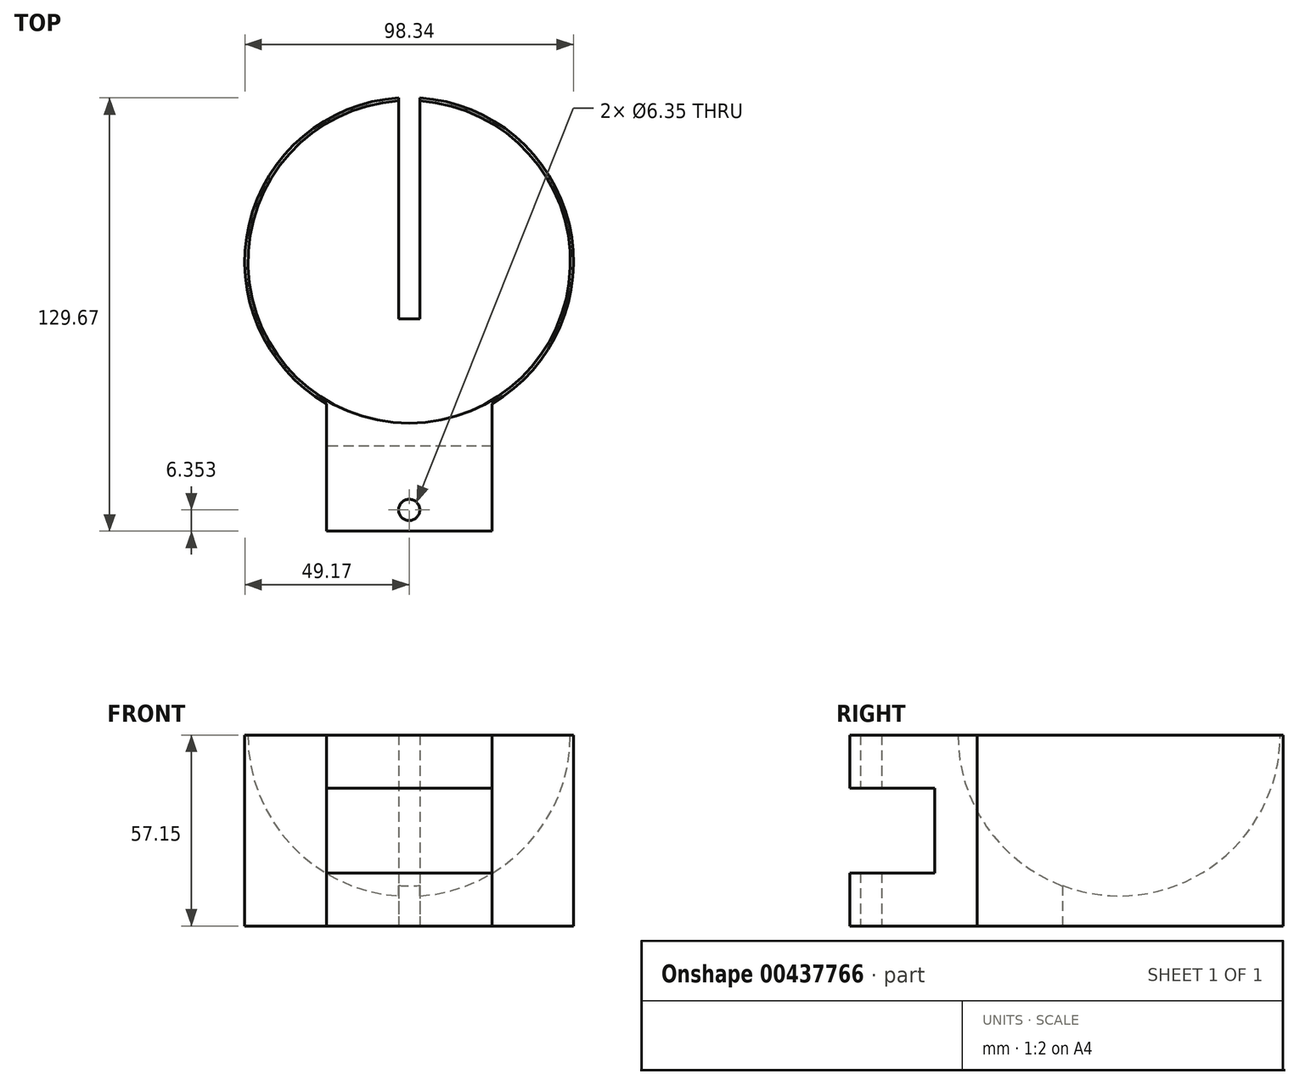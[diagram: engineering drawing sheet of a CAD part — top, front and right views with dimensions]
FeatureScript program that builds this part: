
annotation { "Feature Type Name" : "Feature", "Feature Type Description" : "" }
export const myFeature = defineFeature(function(context is Context, id is Id, definition is map)
    precondition{}
    {
        {
            var Q0;
            Q0=qCreatedBy(makeId("Top.planeOp"),FACE);
            var sketch = newSketch(context, id + "F0", { "sketchPlane" : qUnion([Q0])});
            skCircle(sketch, "E0", {"center": v(0, 0) * mm, "radius": 49.17 * mm});
            skSolve(sketch);
        }
        {
            var Q0;
            Q0 = qSketchRegion(id + "F0", true);
            extrude(context, id + "F1", {"entities" : qUnion([Q0]), "depth" : 57.15 * mm});
        }
        {
            var Q0;
            Q0=qCreatedBy(makeId("Front.planeOp"),FACE);
            var sketch = newSketch(context, id + "F2", { "sketchPlane" : qUnion([Q0])});
            skArc(sketch, "E1", {"start": v(-48.26, 57.15) * mm, "mid": v(-34.12, 23.03) * mm, "end": v(0, 8.9) * mm});
            skLineSegment(sketch, "E2", {"start": v(-48.26, 57.15) * mm, "end": v(0, 57.15) * mm});
            skLineSegment(sketch, "E3", {"start": v(0, 57.15) * mm, "end": v(0, 8.9) * mm});
            skSolve(sketch);
        }
        {
            var Q0;
            Q0 = qSketchRegion(id + "F2", true);
            var Q1;
            Q1=sQuery(id+"F2.wireOp",EDGE,"E3");
            revolve(context, id + "F3", {"operationType" : NewBodyOperationType.REMOVE, "entities" : qUnion([Q0]), "axis" : qUnion([Q1]), "revolveType" : RevolveType.FULL, "oppositeDirection" : true});
        }
        {
            var Q0;
            Q0=qCreatedBy(makeId("Front.planeOp"),FACE);
            var sketch = newSketch(context, id + "F4", { "sketchPlane" : qUnion([Q0])});
            skLineSegment(sketch, "E4.bottom", {"start": v(3.17, 57.15) * mm, "end": v(-3.18, 57.15) * mm});
            skLineSegment(sketch, "E4.top", {"start": v(3.18, 0) * mm, "end": v(-3.17, 0) * mm});
            skLineSegment(sketch, "E4.left", {"start": v(3.18, 57.15) * mm, "end": v(3.18, 0) * mm});
            skLineSegment(sketch, "E4.right", {"start": v(-3.18, 57.15) * mm, "end": v(-3.17, 0) * mm});
            skSolve(sketch);
        }
        {
            var Q0;
            Q0 = qSketchRegion(id + "F4", true);
            extrude(context, id + "F5", {"entities" : qUnion([Q0]), "operationType" : NewBodyOperationType.REMOVE, "oppositeDirection" : true, "depth" : 127 * mm, "hasSecondDirection" : true, "secondDirectionOppositeDirection" : false, "secondDirectionDepth" : 17.02 * mm});
        }
        {
            var Q0;
            Q0=qCreatedBy(makeId("Top.planeOp"),FACE);
            var sketch = newSketch(context, id + "F6", { "sketchPlane" : qUnion([Q0])});
            skArc(sketch, "E5", {"start": v(-24.74, -42.5) * mm, "mid": v(0, -49.17) * mm, "end": v(24.74, -42.5) * mm});
            skLineSegment(sketch, "E6.top", {"start": v(-24.74, -80.6) * mm, "end": v(24.74, -80.6) * mm});
            skLineSegment(sketch, "E6.left", {"start": v(-24.74, -42.5) * mm, "end": v(-24.74, -80.6) * mm});
            skLineSegment(sketch, "E6.right", {"start": v(24.74, -42.5) * mm, "end": v(24.74, -80.6) * mm});
            skPoint(sketch, "E7.orphan", {"position": v(24.74, 80.6) * mm});
            skPoint(sketch, "E8.orphan", {"position": v(-24.74, 80.6) * mm});
            skCircle(sketch, "E9", {"center": v(0, -74.25) * mm, "radius": 3.18 * mm});
            skSolve(sketch);
        }
        {
            var Q0;
            Q0 = qSketchRegion(id + "F6", true);
            extrude(context, id + "F7", {"entities" : qUnion([Q0]), "operationType" : NewBodyOperationType.ADD, "depth" : 57.15 * mm});
        }
        {
            var Q0;
            Q0=makeQuery(id+"F7.opExtrude","SWEPT_FACE",FACE,{"disambiguationData":[OSD([sQuery(id+"F6.wireOp",EDGE,"E6.left")])]});
            var sketch = newSketch(context, id + "F8", { "sketchPlane" : qUnion([Q0])});
            skLineSegment(sketch, "E10.bottom", {"start": v(80.6, 15.88) * mm, "end": v(55.2, 15.88) * mm});
            skLineSegment(sketch, "E10.top", {"start": v(80.6, 41.28) * mm, "end": v(55.2, 41.28) * mm});
            skLineSegment(sketch, "E10.left", {"start": v(80.6, 15.88) * mm, "end": v(80.6, 41.28) * mm});
            skLineSegment(sketch, "E10.right", {"start": v(55.2, 15.88) * mm, "end": v(55.2, 41.28) * mm});
            skSolve(sketch);
        }
        {
            var Q0;
            Q0 = qSketchRegion(id + "F8", true);
            extrude(context, id + "F9", {"entities" : qUnion([Q0]), "operationType" : NewBodyOperationType.REMOVE, "oppositeDirection" : true, "depth" : 50.8 * mm});
        }
    });
